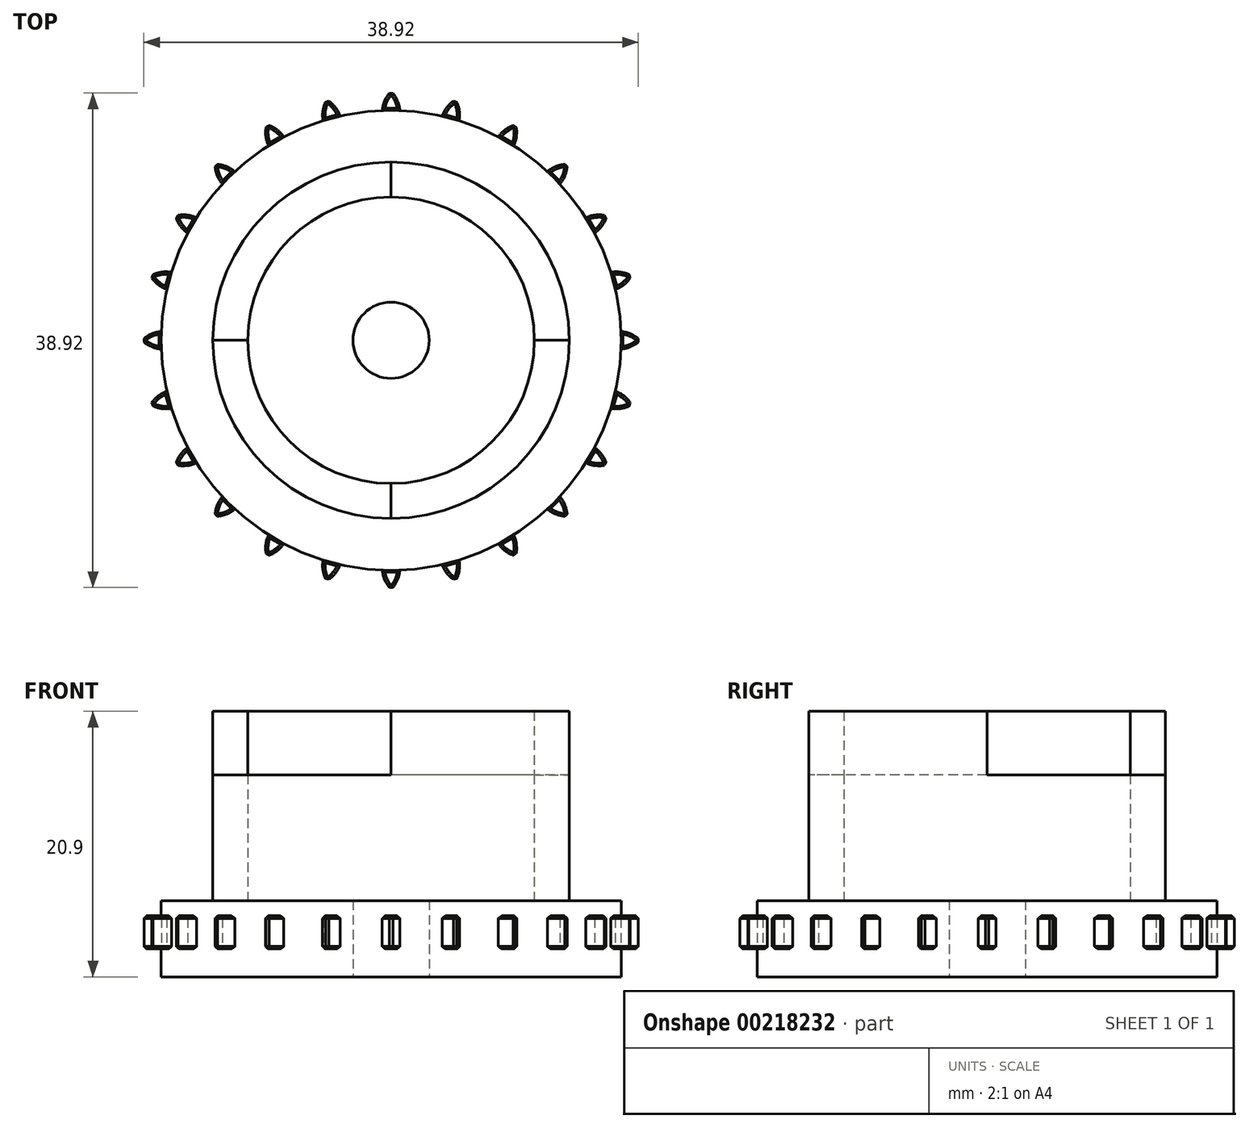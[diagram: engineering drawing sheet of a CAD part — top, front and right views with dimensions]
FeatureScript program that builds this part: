
annotation { "Feature Type Name" : "Feature", "Feature Type Description" : "" }
export const myFeature = defineFeature(function(context is Context, id is Id, definition is map)
    precondition{}
    {
        {
            var Q0;
            Q0=qCreatedBy(makeId("Top.planeOp"),FACE);
            var sketch = newSketch(context, id + "F0", { "sketchPlane" : qUnion([Q0])});
            skCircle(sketch, "E0", {"center": v(0, 0) * mm, "radius": 18.1 * mm});
            skLineSegment(sketch, "E1", {"start": v(0, 0) * mm, "end": v(18.1, 0) * mm});
            skSolve(sketch);
        }
        {
            var Q0;
            Q0=makeQuery(id+"F0.imprint","IMPRINT",FACE,{"disambiguationData":[TD([[makeQuery(id+"F0.imprint","IMPRINT",EDGE,{"derivedFrom":sQuery(id+"F0.wireOp",EDGE,"E0")}),1.0]])]});
            extrude(context, id + "F1", {"entities" : qUnion([Q0]), "depth" : 6 * mm});
        }
        {
            var Q0;
            Q0=qCreatedBy(makeId("Top.planeOp"),FACE);
            cPlane(context, id + "F2", {"entities" : qUnion([Q0]), "cplaneType" : CPlaneType.OFFSET, "offset" : 2.2 * mm, "width" : 150 * mm, "height" : 150 * mm});
        }
        {
            var Q0;
            Q0=qCreatedBy(id+"F2.planeOp",FACE);
            var sketch = newSketch(context, id + "F3", { "sketchPlane" : qUnion([Q0])});
            skLineSegment(sketch, "E2", {"start": v(-3.73, 18.1) * mm, "end": v(8.98, 18.1) * mm, "construction": true});
            skLineSegment(sketch, "E3", {"start": v(-2.65, 17.9) * mm, "end": v(3.22, 17.9) * mm, "construction": true});
            skCircle(sketch, "E4", {"center": v(-1.7, 17.9) * mm, "radius": 2.4 * mm, "construction": true});
            skLineSegment(sketch, "E5", {"start": v(-3.15, 19.45) * mm, "end": v(2.93, 19.45) * mm, "construction": true});
            skLineSegment(sketch, "E6", {"start": v(0.7, 13.77) * mm, "end": v(0.7, 11.3) * mm, "construction": true});
            skLineSegment(sketch, "E7.MirrorCS", {"start": v(3.15, 19.45) * mm, "end": v(-2.93, 19.45) * mm, "construction": true});
            skLineSegment(sketch, "E8", {"start": v(0, 19.45) * mm, "end": v(0.14, 19.45) * mm});
            skFitSpline(sketch, "E9", {"points": [v(0.14, 19.45) * mm, v(0.3, 19.24) * mm, v(0.53, 18.8) * mm, v(0.65, 18.44) * mm, v(0.7, 18.05) * mm], "startDerivative": vector(0.73, -0.9) * mm, "endDerivative": vector(0.2, -1.49) * mm});
            skFitSpline(sketch, "E10.MirrorCS", {"points": [v(-0.14, 19.45) * mm, v(-0.3, 19.24) * mm, v(-0.53, 18.8) * mm, v(-0.65, 18.44) * mm, v(-0.7, 18.05) * mm], "startDerivative": vector(-0.73, -0.9) * mm, "endDerivative": vector(-0.2, -1.49) * mm});
            skLineSegment(sketch, "E11", {"start": v(-0.7, 18.05) * mm, "end": v(0.7, 18.05) * mm});
            skLineSegment(sketch, "E12", {"start": v(-0.14, 19.45) * mm, "end": v(0.14, 19.45) * mm});
            skSolve(sketch);
        }
        {
            var Q0;
            {var subQ0=sQuery(id+"F3.wireOp",EDGE,"E9");Q0=makeQuery(id+"F3.imprint","IMPRINT",FACE,{"disambiguationData":[TD([[makeQuery(id+"F3.imprint","IMPRINT",EDGE,{"derivedFrom":subQ0}),-1.0]])]});}
            extrude(context, id + "F4", {"entities" : qUnion([Q0]), "depth" : 2.6 * mm});
        }
        {
            var Q0;
            Q0=makeQuery(id+"F4.opExtrude","CAP_FACE",FACE,{"disambiguationData":[OSD([sQuery(id+"F3.wireOp",EDGE,"E9"),sQuery(id+"F3.wireOp",EDGE,"E10.MirrorCS"),sQuery(id+"F3.wireOp",EDGE,"E11"),sQuery(id+"F3.wireOp",EDGE,"E12")])],"isStart":true});
            var Q1;
            Q1=makeQuery(id+"F4.opExtrude","CAP_FACE",FACE,{"disambiguationData":[OSD([sQuery(id+"F3.wireOp",EDGE,"E9"),sQuery(id+"F3.wireOp",EDGE,"E10.MirrorCS"),sQuery(id+"F3.wireOp",EDGE,"E11"),sQuery(id+"F3.wireOp",EDGE,"E12")])],"isStart":false});
            chamfer(context, id + "F5", {"entities" : qUnion([Q0, Q1]), "width" : 0.2 * mm, "tangentPropagation" : true});
        }
        {
            var Q0;
            Q0=makeQuery(id+"F4.opExtrude","SWEPT_BODY",BODY,{"disambiguationData":[OSD([sQuery(id+"F3.wireOp",EDGE,"E9"),sQuery(id+"F3.wireOp",EDGE,"E10.MirrorCS"),sQuery(id+"F3.wireOp",EDGE,"E11"),sQuery(id+"F3.wireOp",EDGE,"E12")])]});
            var Q1;
            Q1=makeQuery(id+"F1.opExtrude","CAP_EDGE",EDGE,{"disambiguationData":[OSD([sQuery(id+"F0.wireOp",EDGE,"E0")])],"isStart":true});
            circularPattern(context, id + "F6", {"operationType" : NewBodyOperationType.ADD, "entities" : qUnion([Q0]), "axis" : qUnion([Q1]), "angle" : 360 * degree, "instanceCount" : 24, "equalSpace" : true});
        }
        {
            var Q0;
            Q0=makeQuery(id+"F1.opExtrude","CAP_FACE",FACE,{"disambiguationData":[OSD([sQuery(id+"F0.wireOp",EDGE,"E0")])],"isStart":false});
            var sketch = newSketch(context, id + "F7", { "sketchPlane" : qUnion([Q0])});
            skCircle(sketch, "E13", {"center": v(0, 0) * mm, "radius": 14.03 * mm});
            skCircle(sketch, "E14", {"center": v(0, 0) * mm, "radius": 11.27 * mm});
            skSolve(sketch);
        }
        {
            var Q0;
            Q0=qSketchRegion(id+"F7",true);
            extrude(context, id + "F8", {"entities" : qUnion([Q0]), "operationType" : NewBodyOperationType.ADD, "depth" : 14.9 * mm});
        }
        {
            var Q0;
            Q0=sQuery(id+"F0.wireOp",VERTEX,"E0.center");
            var Q1;
            Q1=makeQuery(id+"F1.opExtrude","SWEPT_BODY",BODY,{"disambiguationData":[OSD([sQuery(id+"F0.wireOp",EDGE,"E0")])]});
            hole(context, id + "F9", {"style" : HoleStyle.SIMPLE, "endStyle" : HoleEndStyle.THROUGH, "oppositeDirection" : true, "holeDiameter" : 6 * mm, "locations" : qUnion([Q0]), "scope" : qUnion([Q1]), "isTappedThrough" : true});
        }
        {
            var Q0;
            Q0=makeQuery(id+"F8.opExtrude","CAP_FACE",FACE,{"disambiguationData":[OSD([sQuery(id+"F7.wireOp",EDGE,"E13")])],"isStart":false});
            var sketch = newSketch(context, id + "F10", { "sketchPlane" : qUnion([Q0])});
            skLineSegment(sketch, "E15", {"start": v(-15.4, 0) * mm, "end": v(17.38, 0) * mm});
            skLineSegment(sketch, "E16", {"start": v(17.38, 0) * mm, "end": v(17.38, 16.12) * mm});
            skLineSegment(sketch, "E17", {"start": v(17.38, 16.12) * mm, "end": v(0, 16.12) * mm});
            skLineSegment(sketch, "E18", {"start": v(0, 16.12) * mm, "end": v(0, -15.3) * mm});
            skLineSegment(sketch, "E19", {"start": v(0, -15.3) * mm, "end": v(-15.4, -15.3) * mm});
            skLineSegment(sketch, "E20", {"start": v(-15.4, -15.3) * mm, "end": v(-15.4, 0) * mm});
            skSolve(sketch);
        }
        {
            var Q0;
            Q0=qSketchRegion(id+"F10",true);
            extrude(context, id + "F11", {"entities" : qUnion([Q0]), "operationType" : NewBodyOperationType.REMOVE, "oppositeDirection" : true, "depth" : 5 * mm});
        }
    });
